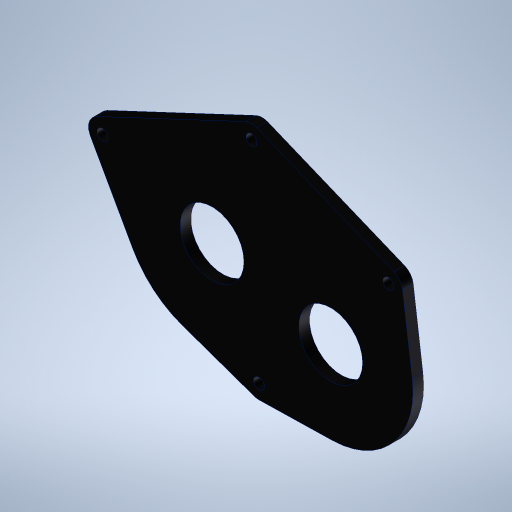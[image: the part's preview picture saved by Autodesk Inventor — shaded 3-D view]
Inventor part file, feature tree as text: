
AUTODESK INVENTOR PART (.ipt)
format: ipt  version: 2024 (Build 280153000, 153)  size: 291,328 bytes
history: native  units: in
note: dims shown in document units (in); Inventor stores cm internally (conversion verified against a paired STEP export)
features: extrude x1, sketch x1
ambient origin geometry x8: Origin, YZ Plane, XZ Plane, XY Plane, X Axis, Y Axis, Z Axis, Center Point
bodies: Body1 (feature_tree)
feature tree (2):
  extrude  "Extrusion2"  Depth=0.188in
  sketch  "Sketch1"  dims[d0=3.0in d1=0.6in d2=2.36in d3=1.5in d4=2.8in d5=1.125in d6=0.813in d8=0.375in d9=2.9in d10=0.1in d12=0.5in d13=0.196in d14=0.0625in d15=0.5in d16=0.196in d17=0.5in d18=0.196in d19=0.5in d20=0.196in d21=0.0625in d22=0.0625in d23=0.0625in d24=0.0625in d27=0.188in d28=0.0in d29=0.5in d30=0.0344in]
